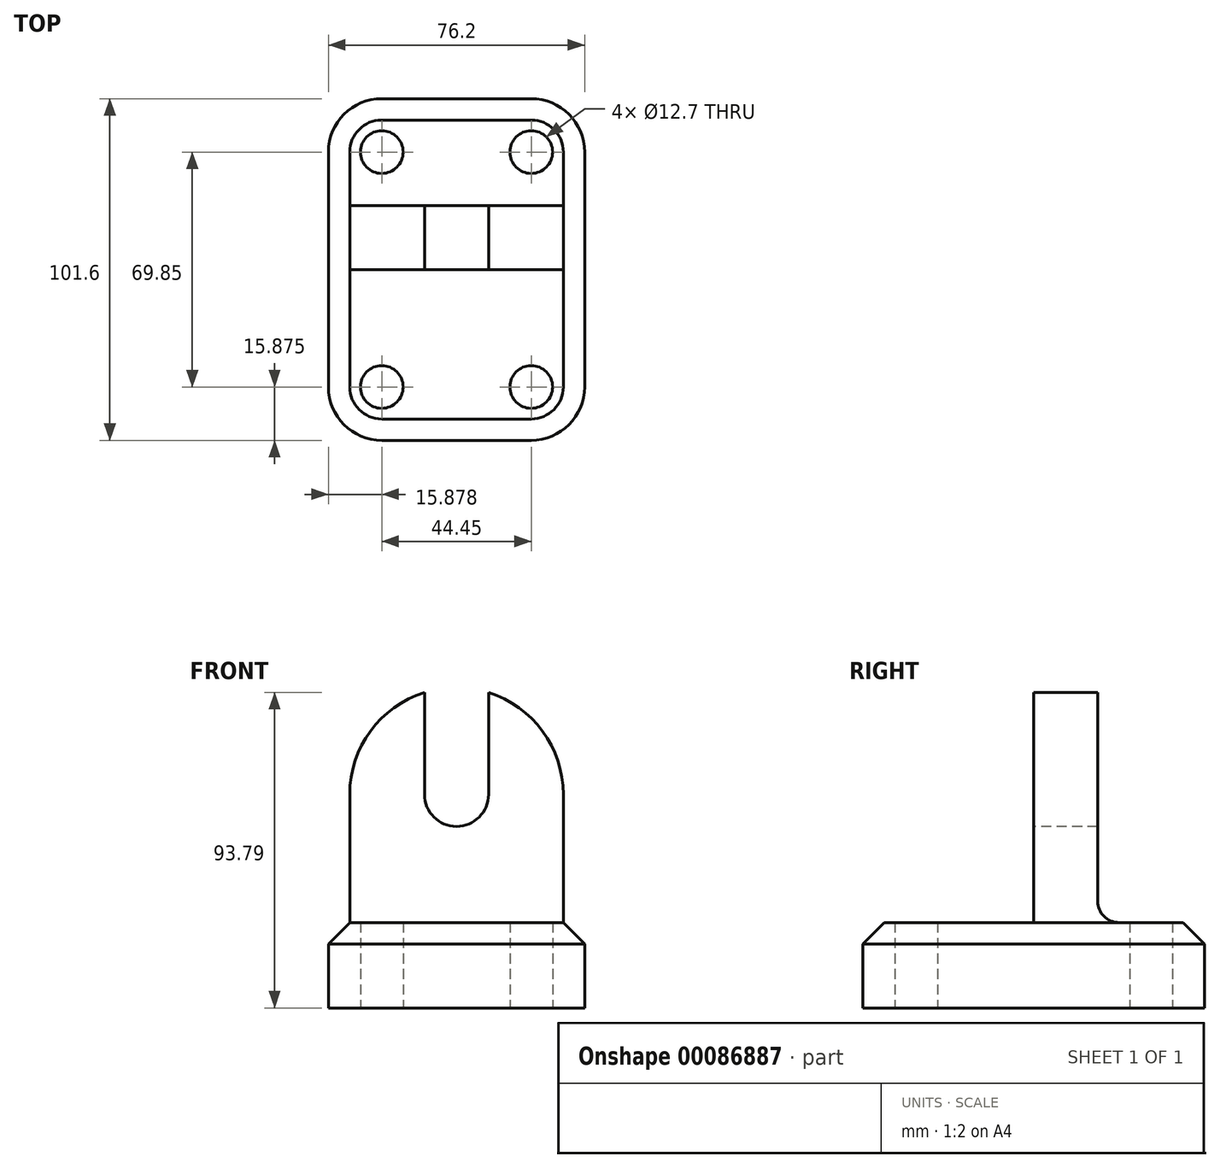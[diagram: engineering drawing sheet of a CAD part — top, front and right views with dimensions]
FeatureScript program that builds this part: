
annotation { "Feature Type Name" : "Feature", "Feature Type Description" : "" }
export const myFeature = defineFeature(function(context is Context, id is Id, definition is map)
    precondition{}
    {
        {
            var Q0;
            Q0=qCreatedBy(makeId("Top.planeOp"),FACE);
            var sketch = newSketch(context, id + "F0", { "sketchPlane" : qUnion([Q0])});
            skLineSegment(sketch, "E0.bottom", {"start": v(-57.7, 83.22) * mm, "end": v(-13.25, 83.22) * mm});
            skLineSegment(sketch, "E0.top", {"start": v(-57.7, -18.38) * mm, "end": v(-13.25, -18.38) * mm});
            skLineSegment(sketch, "E0.left", {"start": v(-73.58, 67.34) * mm, "end": v(-73.58, -2.5) * mm});
            skLineSegment(sketch, "E0.right", {"start": v(2.62, 67.34) * mm, "end": v(2.62, -2.5) * mm});
            skPoint(sketch, "E1.visualSharp", {"position": v(-73.58, 83.22) * mm});
            skArc(sketch, "E1.filletArc", {"start": v(-57.7, 83.22) * mm, "mid": v(-68.93, 78.57) * mm, "end": v(-73.58, 67.34) * mm});
            skPoint(sketch, "E2.visualSharp", {"position": v(2.62, 83.22) * mm});
            skArc(sketch, "E2.filletArc", {"start": v(2.62, 67.34) * mm, "mid": v(-2.03, 78.57) * mm, "end": v(-13.25, 83.22) * mm});
            skPoint(sketch, "E3.visualSharp", {"position": v(-73.58, -18.38) * mm});
            skArc(sketch, "E3.filletArc", {"start": v(-73.58, -2.5) * mm, "mid": v(-68.93, -13.73) * mm, "end": v(-57.7, -18.38) * mm});
            skPoint(sketch, "E4.visualSharp", {"position": v(2.62, -18.38) * mm});
            skArc(sketch, "E4.filletArc", {"start": v(-13.25, -18.38) * mm, "mid": v(-2.03, -13.73) * mm, "end": v(2.62, -2.5) * mm});
            skCircle(sketch, "E5", {"center": v(-57.7, -2.5) * mm, "radius": 6.35 * mm});
            skCircle(sketch, "E6", {"center": v(-13.25, -2.5) * mm, "radius": 6.35 * mm});
            skCircle(sketch, "E7", {"center": v(-13.25, 67.34) * mm, "radius": 6.35 * mm});
            skCircle(sketch, "E8", {"center": v(-57.7, 67.34) * mm, "radius": 6.35 * mm});
            skLineSegment(sketch, "E9", {"start": v(-73.58, -18.38) * mm, "end": v(-73.58, 32.42) * mm});
            skPoint(sketch, "E10", {"position": v(-73.58, 32.42) * mm});
            skPoint(sketch, "E11", {"position": v(2.62, 32.42) * mm});
            skLineSegment(sketch, "E12", {"start": v(-73.58, 32.42) * mm, "end": v(-73.58, 50.74) * mm});
            skLineSegment(sketch, "E13.bottom", {"start": v(-73.58, 32.42) * mm, "end": v(2.62, 32.42) * mm});
            skLineSegment(sketch, "E13.top", {"start": v(-73.58, 51.47) * mm, "end": v(2.62, 51.47) * mm});
            skLineSegment(sketch, "E13.left", {"start": v(-73.58, 32.42) * mm, "end": v(-73.58, 51.47) * mm});
            skLineSegment(sketch, "E13.right", {"start": v(2.62, 32.42) * mm, "end": v(2.62, 51.47) * mm});
            skSolve(sketch);
        }
        {
            var Q0;
            Q0=makeQuery(id+"F0.imprint","IMPRINT",FACE,{"disambiguationData":[TD([[makeQuery(id+"F0.imprint","IMPRINT",EDGE,{"derivedFrom":sQuery(id+"F0.wireOp",EDGE,"E0.bottom")}),-1.0]])]});
            var Q1;
            {var subQ0=sQuery(id+"F0.wireOp",EDGE,"E13.bottom");Q1=makeQuery(id+"F0.imprint","IMPRINT",FACE,{"disambiguationData":[TD([[makeQuery(id+"F0.imprint","IMPRINT",EDGE,{"derivedFrom":subQ0}),1.0]])]});}
            var Q2;
            Q2=makeQuery(id+"F0.imprint","IMPRINT",FACE,{"disambiguationData":[TD([[makeQuery(id+"F0.imprint","IMPRINT",EDGE,{"derivedFrom":sQuery(id+"F0.wireOp",EDGE,"E0.top")}),1.0]])]});
            extrude(context, id + "F1", {"entities" : qUnion([Q0, Q1, Q2]), "depth" : 25.4 * mm});
        }
        {
            var Q0;
            Q0=makeQuery(id+"F1.opExtrude","CAP_EDGE",EDGE,{"disambiguationData":[OSD([sQuery(id+"F0.wireOp",EDGE,"E0.bottom")])],"isStart":false});
            chamfer(context, id + "F2", {"entities" : qUnion([Q0]), "width" : 6.35 * mm, "tangentPropagation" : true});
        }
        {
            var Q0;
            Q0=makeQuery(id+"F1.opExtrude","CAP_FACE",FACE,{"disambiguationData":[OSD([sQuery(id+"F0.wireOp",EDGE,"E0.bottom"),sQuery(id+"F0.wireOp",EDGE,"E0.top"),sQuery(id+"F0.wireOp",EDGE,"E0.left"),sQuery(id+"F0.wireOp",EDGE,"E0.right"),sQuery(id+"F0.wireOp",EDGE,"E1.filletArc"),sQuery(id+"F0.wireOp",EDGE,"E2.filletArc"),sQuery(id+"F0.wireOp",EDGE,"E3.filletArc"),sQuery(id+"F0.wireOp",EDGE,"E4.filletArc"),sQuery(id+"F0.wireOp",EDGE,"E5"),sQuery(id+"F0.wireOp",EDGE,"E6"),sQuery(id+"F0.wireOp",EDGE,"E7"),sQuery(id+"F0.wireOp",EDGE,"E8"),sQuery(id+"F0.wireOp",EDGE,"E9"),sQuery(id+"F0.wireOp",EDGE,"E13.left"),sQuery(id+"F0.wireOp",EDGE,"E13.right")])],"isStart":false});
            var sketch = newSketch(context, id + "F3", { "sketchPlane" : qUnion([Q0])});
            skPoint(sketch, "E14", {"position": v(-67.23, 32.42) * mm});
            skPoint(sketch, "E15", {"position": v(-67.23, 51.47) * mm});
            skPoint(sketch, "E16", {"position": v(-3.73, 51.47) * mm});
            skPoint(sketch, "E17", {"position": v(-3.73, 32.42) * mm});
            skLineSegment(sketch, "E18.bottom", {"start": v(-67.23, 51.47) * mm, "end": v(-3.73, 51.47) * mm});
            skLineSegment(sketch, "E18.top", {"start": v(-67.23, 32.42) * mm, "end": v(-3.73, 32.42) * mm});
            skLineSegment(sketch, "E18.left", {"start": v(-67.23, 51.47) * mm, "end": v(-67.23, 32.42) * mm});
            skLineSegment(sketch, "E18.right", {"start": v(-3.73, 51.47) * mm, "end": v(-3.73, 32.42) * mm});
            skSolve(sketch);
        }
        {
            var Q0;
            Q0=makeQuery(id+"F3.imprint","IMPRINT",FACE,{"disambiguationData":[TD([[makeQuery(id+"F3.imprint","IMPRINT",EDGE,{"derivedFrom":sQuery(id+"F3.wireOp",EDGE,"E18.bottom")}),-1.0]])]});
            extrude(context, id + "F4", {"entities" : qUnion([Q0]), "operationType" : NewBodyOperationType.ADD, "depth" : 95.25 * mm});
        }
        {
            var Q0;
            Q0=makeQuery(id+"F4.opExtrude","SWEPT_FACE",FACE,{"disambiguationData":[OSD([sQuery(id+"F3.wireOp",EDGE,"E18.top")])]});
            var sketch = newSketch(context, id + "F5", { "sketchPlane" : qUnion([Q0])});
            skPoint(sketch, "E19", {"position": v(-35.48, 63.5) * mm});
            skCircle(sketch, "E20", {"center": v(-35.48, 63.5) * mm, "radius": 9.53 * mm});
            skArc(sketch, "E21", {"start": v(-3.73, 63.5) * mm, "mid": v(-35.48, 95.25) * mm, "end": v(-67.23, 63.5) * mm});
            skLineSegment(sketch, "E22", {"start": v(-45, 63.5) * mm, "end": v(-45, 93.79) * mm});
            skLineSegment(sketch, "E23", {"start": v(-35.48, 63.5) * mm, "end": v(-25.95, 63.5) * mm});
            skLineSegment(sketch, "E24", {"start": v(-25.95, 63.5) * mm, "end": v(-25.95, 93.79) * mm});
            skSolve(sketch);
        }
        {
            var Q0;
            {var subQ0=sQuery(id+"F3.wireOp",EDGE,"E18.top");var subQ1=makeQuery(id+"F4.opExtrude","CAP_EDGE",EDGE,{"disambiguationData":[OSD([subQ0])],"isStart":false});Q0=makeQuery(id+"F5.imprint","IMPRINT",FACE,{"disambiguationData":[TD([[makeQuery(id+"F5.imprint","IMPRINT",EDGE,{"derivedFrom":subQ1}),-1.0]])]});}
            var Q1;
            {var subQ0=sQuery(id+"F5.wireOp",EDGE,"E22");Q1=makeQuery(id+"F5.imprint","IMPRINT",FACE,{"disambiguationData":[TD([[makeQuery(id+"F5.imprint","IMPRINT",EDGE,{"derivedFrom":subQ0}),-1.0]])]});}
            var Q2;
            {var subQ0=sQuery(id+"F5.wireOp",EDGE,"E20");var subQ1=makeQuery(id+"F5.imprint","INTERSECT",VERTEX,{"derivedFrom":[subQ0,sQuery(id+"F5.wireOp",EDGE,"E22")]});Q2=makeQuery(id+"F5.imprint","IMPRINT",FACE,{"disambiguationData":[TD([[makeQuery(id+"F5.imprint","IMPRINT",EDGE,{"disambiguationData":[TD([[subQ1,1.0]])],"derivedFrom":subQ0}),1.0]])]});}
            extrude(context, id + "F6", {"entities" : qUnion([Q0, Q1, Q2]), "operationType" : NewBodyOperationType.REMOVE, "oppositeDirection" : true, "depth" : 25.4 * mm});
        }
        {
            var Q0;
            Q0=makeQuery(id+"F4.opExtrude","CAP_EDGE",EDGE,{"disambiguationData":[OSD([sQuery(id+"F3.wireOp",EDGE,"E18.bottom")])],"isStart":true});
            var Q1;
            Q1=makeQuery(id+"F4.opExtrude","CAP_EDGE",EDGE,{"disambiguationData":[OSD([sQuery(id+"F3.wireOp",EDGE,"E18.top")])],"isStart":true});
            fillet(context, id + "F7", {"entities" : qUnion([Q0, Q1]), "radius" : 6.35 * mm, "tangentPropagation" : true, "allowEdgeOverflow" : false});
        }
    });
